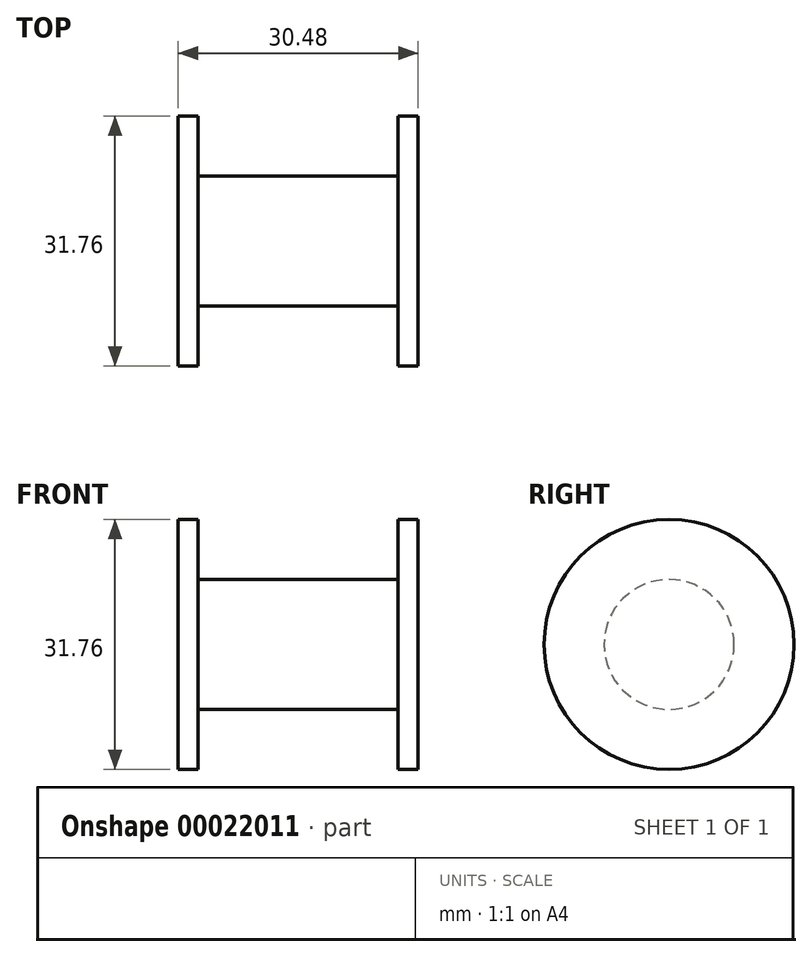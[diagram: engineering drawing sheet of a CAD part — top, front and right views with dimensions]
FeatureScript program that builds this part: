
annotation { "Feature Type Name" : "Feature", "Feature Type Description" : "" }
export const myFeature = defineFeature(function(context is Context, id is Id, definition is map)
    precondition{}
    {
        {
            var Q0;
            Q0=qCreatedBy(makeId("Right.planeOp"),FACE);
            var sketch = newSketch(context, id + "F0", { "sketchPlane" : qUnion([Q0])});
            skCircle(sketch, "E0", {"center": v(0, 0) * mm, "radius": 15.88 * mm});
            skSolve(sketch);
        }
        {
            var Q0;
            Q0 = qSketchRegion(id + "F0", true);
            extrude(context, id + "F1", {"entities" : qUnion([Q0]), "depth" : 30.48 * mm});
        }
        {
            var Q0;
            Q0=makeQuery(id+"F1.opExtrude","CAP_FACE",FACE,{"disambiguationData":[OSD([sQuery(id+"F0.wireOp",EDGE,"E0")])],"isStart":false});
            cPlane(context, id + "F2", {"entities" : qUnion([Q0]), "cplaneType" : CPlaneType.OFFSET, "offset" : 2.54 * mm, "oppositeDirection" : true, "width" : 152.4 * mm, "height" : 152.4 * mm});
        }
        {
            var Q0;
            Q0=qCreatedBy(id+"F2.planeOp",FACE);
            var sketch = newSketch(context, id + "F3", { "sketchPlane" : qUnion([Q0])});
            skCircle(sketch, "E1", {"center": v(0, 0) * mm, "radius": 23.5 * mm});
            skSolve(sketch);
        }
        {
            var Q0;
            Q0 = qSketchRegion(id + "F3", true);
            extrude(context, id + "F4", {"entities" : qUnion([Q0]), "operationType" : NewBodyOperationType.REMOVE, "oppositeDirection" : true, "depth" : 25.4 * mm});
        }
        {
            var Q0;
            Q0=makeQuery(id+"F4.boolean.opBoolean","COPY",FACE,{"derivedFrom":makeQuery(id+"F4.opExtrude","CAP_FACE",FACE,{"disambiguationData":[OSD([sQuery(id+"F3.wireOp",EDGE,"E1")])],"isStart":false})});
            var sketch = newSketch(context, id + "F5", { "sketchPlane" : qUnion([Q0])});
            skCircle(sketch, "E2", {"center": v(0, 0) * mm, "radius": 8.26 * mm});
            skSolve(sketch);
        }
        {
            var Q0;
            Q0 = qSketchRegion(id + "F5", true);
            extrude(context, id + "F6", {"entities" : qUnion([Q0]), "operationType" : NewBodyOperationType.ADD, "depth" : 25.4 * mm});
        }
    });
